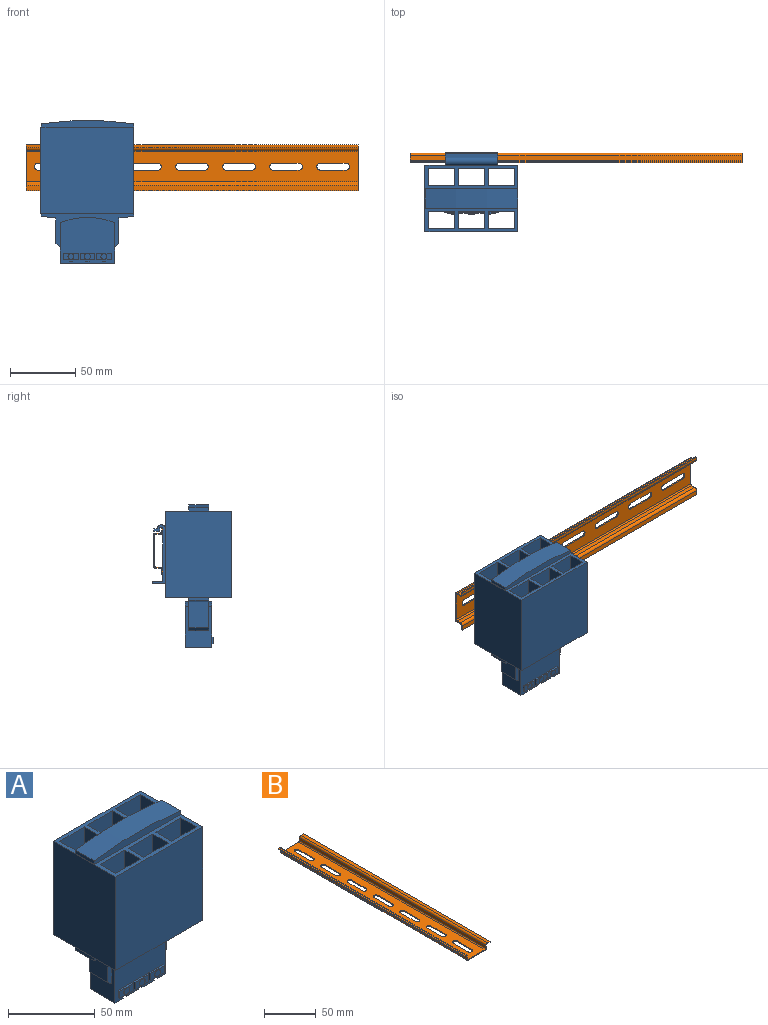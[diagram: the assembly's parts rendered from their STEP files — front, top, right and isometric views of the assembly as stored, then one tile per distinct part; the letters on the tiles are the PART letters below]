
ASSEMBLY  parts=2 mates=1
PART A: 105 faces, bbox 71.1x61x109.2 mm
  f0: cylinder r=246.65mm len=70.61mm, axis (0,-1,0), area 1079.8mm2, adj f9,f10,f11,f12
  f1: plane 40.01x1.91mm, normal (0,1,0), area 76.2mm2, adj f2,f13,f14,f15
  f2: plane 40.01x8.26mm, normal (0,0,1), area 330.2mm2, adj f1,f3,f13,f15
  f3: plane 40.01x40.01mm, normal (0,1,0), area 1600.4mm2, adj f2,f4,f13,f15
  f4: cylinder r=1.27mm len=40.01mm, axis (-1,0,0), area 159.6mm2, adj f3,f5,f13,f15
  f5: plane 40.01x1.91mm, normal (0,-1,0), area 76.2mm2, adj f4,f6,f13,f15
  f6: plane 40.01x4.45mm, normal (0,0,-1), area 177.8mm2, adj f5,f7,f13,f15
  f7: plane 40.01x1.91mm, normal (0,1,0), area 76.2mm2, adj f6,f8,f13,f15
  f8: plane 40.01x2.54mm, normal (0,0,1), area 101.6mm2, adj f7,f13,f15,f16
  f9: plane 70.61x5.08mm, normal (0,1,0), area 299mm2, adj f0,f10,f12,f17
  f10: plane 15.24x2.54mm, normal (-1,0,0), area 38.7mm2, adj f0,f9,f11,f17
  f11: plane 70.61x5.08mm, normal (0,-1,0), area 299mm2, adj f0,f10,f12,f17
  f12: plane 15.24x2.54mm, normal (1,0,0), area 38.7mm2, adj f0,f9,f11,f17
  f13: plane 45.09x10.16mm, normal (1,0,0), area 117.3mm2, adj f1,f2,f3,f4,f5,f6,f7,f8
  f14: plane 40.01x10.16mm, normal (0,0,-1), area 406.5mm2, adj f1,f13,f15,f20
  f15: plane 45.09x10.16mm, normal (-1,0,0), area 117.3mm2, adj f1,f2,f3,f4,f5,f6,f7,f8
  f16: cylinder r=3.17mm len=40.01mm, axis (-1,0,0), area 399mm2, adj f8,f13,f15,f20
  f17: plane 71.12x50.8mm, normal (0,0,1), area 988.4mm2, adj f9,f10,f11,f12,f20,f21,f22,f23
  f18: plane 4.57x4.57mm, normal (0,-1,0), area 16.4mm2, adj f48
  f19: plane 4.57x4.57mm, normal (0,-1,0), area 16.4mm2, adj f49
  f20: plane 71.12x66.04mm, normal (0,1,0), area 3020.2mm2, adj f13,f14,f15,f16,f17,f21,f23,f54
  f21: plane 66.04x50.8mm, normal (-1,0,0), area 3354.8mm2, adj f17,f20,f22,f54
  f22: plane 71.12x66.04mm, normal (0,-1,0), area 4696.8mm2, adj f17,f21,f23,f54
  f23: plane 66.04x50.8mm, normal (1,0,0), area 3354.8mm2, adj f17,f20,f22,f54
  f24: plane 66.04x12.7mm, normal (1,0,0), area 838.7mm2, adj f17,f25,f27,f54
  f25: plane 66.04x20.32mm, normal (0,-1,0), area 1341.9mm2, adj f17,f24,f26,f54
  f26: plane 66.04x12.7mm, normal (-1,0,0), area 838.7mm2, adj f17,f25,f27,f54
  f27: plane 66.04x20.32mm, normal (0,1,0), area 1341.9mm2, adj f17,f24,f26,f54
  f28: plane 66.04x12.7mm, normal (1,0,0), area 838.7mm2, adj f17,f29,f31,f54
  f29: plane 66.04x20.32mm, normal (0,-1,0), area 1341.9mm2, adj f17,f28,f30,f54
  f30: plane 66.04x12.7mm, normal (-1,0,0), area 838.7mm2, adj f17,f29,f31,f54
  f31: plane 66.04x20.32mm, normal (0,1,0), area 1341.9mm2, adj f17,f28,f30,f54
  f32: plane 66.04x12.7mm, normal (1,0,0), area 838.7mm2, adj f17,f33,f35,f54
  f33: plane 66.04x20.32mm, normal (0,-1,0), area 1341.9mm2, adj f17,f32,f34,f54
  f34: plane 66.04x12.7mm, normal (-1,0,0), area 838.7mm2, adj f17,f33,f35,f54
  f35: plane 66.04x20.32mm, normal (0,1,0), area 1341.9mm2, adj f17,f32,f34,f54
  f36: plane 66.04x12.7mm, normal (1,0,0), area 838.7mm2, adj f17,f37,f39,f54
  f37: plane 66.04x20.32mm, normal (0,-1,0), area 1341.9mm2, adj f17,f36,f38,f54
  f38: plane 66.04x12.7mm, normal (-1,0,0), area 838.7mm2, adj f17,f37,f39,f54
  f39: plane 66.04x20.32mm, normal (0,1,0), area 1341.9mm2, adj f17,f36,f38,f54
  f40: plane 66.04x12.7mm, normal (1,0,0), area 838.7mm2, adj f17,f41,f43,f54
  f41: plane 66.04x20.32mm, normal (0,-1,0), area 1341.9mm2, adj f17,f40,f42,f54
  f42: plane 66.04x12.7mm, normal (-1,0,0), area 838.7mm2, adj f17,f41,f43,f54
  f43: plane 66.04x20.32mm, normal (0,1,0), area 1341.9mm2, adj f17,f40,f42,f54
  f44: plane 66.04x12.7mm, normal (1,0,0), area 838.7mm2, adj f17,f45,f47,f54
  f45: plane 66.04x20.32mm, normal (0,-1,0), area 1341.9mm2, adj f17,f44,f46,f54
  f46: plane 66.04x12.7mm, normal (-1,0,0), area 838.7mm2, adj f17,f45,f47,f54
  f47: plane 66.04x20.32mm, normal (0,1,0), area 1341.9mm2, adj f17,f44,f46,f54
  f48: cylinder r=2.29mm len=4.57mm, axis (0,-1,0), area 3.6mm2, adj f18,f59
  f49: cylinder r=2.29mm len=4.57mm, axis (0,-1,0), area 3.6mm2, adj f19,f60
  f50: plane 15.24x2.55mm, normal (0.66,0,-0.75), area 51.8mm2, adj f51,f67,f68,f69
  f51: plane 19.67x15.24mm, normal (1,0,0), area 299.7mm2, adj f50,f52,f67,f69
  f52: plane 15.24x11.18mm, normal (0.11,0,-0.99), area 171.3mm2, adj f51,f53,f67,f69
  f53: plane 15.24x2.29mm, normal (1,0,0), area 35mm2, adj f52,f54,f67,f69
  f54: plane 71.12x50.8mm, normal (0,0,-1), area 988.4mm2, adj f20,f21,f22,f23,f24,f25,f26,f27
  f55: plane 15.24x2.29mm, normal (-1,0,0), area 35mm2, adj f54,f56,f67,f69
  f56: plane 15.24x11.18mm, normal (-0.11,0,-0.99), area 171.3mm2, adj f55,f57,f67,f69
  f57: plane 19.67x15.24mm, normal (-1,0,0), area 299.7mm2, adj f56,f58,f67,f69
  f58: plane 15.24x2.55mm, normal (-0.66,0,-0.75), area 51.8mm2, adj f57,f65,f67,f69
  f59: plane 11.32x5.08mm, normal (0,-1,0), area 41.1mm2, adj f48,f76,f77,f78,f79
  f60: plane 11.32x5.08mm, normal (0,-1,0), area 41.1mm2, adj f49,f80,f81,f82,f83
  f61: plane 2.54x2.54mm, normal (0,1,0), area 6.5mm2, adj f62,f84,f85,f86
  f62: plane 2.54x2.54mm, normal (0,0,-1), area 6.5mm2, adj f61,f72,f84,f86
  f63: plane 2.54x2.54mm, normal (0,1,0), area 6.5mm2, adj f64,f87,f88,f89
  f64: plane 2.54x2.54mm, normal (0,0,-1), area 6.5mm2, adj f63,f71,f87,f89
  f65: plane 15.24x0.8mm, normal (0,0,-1), area 12.1mm2, adj f58,f67,f69,f90
  f66: cylinder r=57.07mm len=41.58mm, axis (0,-1,0), area 108.1mm2, adj f69,f70,f90,f92
  f67: plane 70.61x25.4mm, normal (0,-1,0), area 411.7mm2, adj f50,f51,f52,f53,f54,f55,f56,f57
  f68: plane 15.24x0.8mm, normal (0,0,-1), area 12.1mm2, adj f50,f67,f69,f92
  f69: plane 70.61x25.4mm, normal (0,1,0), area 411.7mm2, adj f50,f51,f52,f53,f54,f55,f56,f57
  f70: plane 41.58x34.98mm, normal (0,1,0), area 1401mm2, adj f66,f90,f92,f93
  f71: plane 3.81x2.54mm, normal (0,-1,0), area 9.7mm2, adj f64,f87,f89,f93
  f72: plane 3.81x2.54mm, normal (0,-1,0), area 9.7mm2, adj f62,f84,f86,f93
  f73: plane 2.54x2.54mm, normal (0,1,0), area 6.5mm2, adj f74,f94,f95,f96
  f74: plane 2.54x2.54mm, normal (0,0,-1), area 6.5mm2, adj f73,f75,f94,f96
  f75: plane 3.81x2.54mm, normal (0,-1,0), area 9.7mm2, adj f74,f93,f94,f96
  f76: plane 5.08x1.27mm, normal (1,0,0), area 6.5mm2, adj f59,f77,f79,f97
  f77: plane 11.32x1.27mm, normal (0,0,1), area 14.4mm2, adj f59,f76,f78,f97
  f78: plane 5.08x1.27mm, normal (-1,0,0), area 6.5mm2, adj f59,f77,f79,f97
  f79: plane 11.32x1.27mm, normal (0,0,-1), area 14.4mm2, adj f59,f76,f78,f97
  f80: plane 5.08x1.27mm, normal (1,0,0), area 6.5mm2, adj f60,f81,f83,f97
  f81: plane 11.32x1.27mm, normal (0,0,1), area 14.4mm2, adj f60,f80,f82,f97
  f82: plane 5.08x1.27mm, normal (-1,0,0), area 6.5mm2, adj f60,f81,f83,f97
  f83: plane 11.32x1.27mm, normal (0,0,-1), area 14.4mm2, adj f60,f80,f82,f97
  f84: plane 15.24x3.81mm, normal (-1,0,0), area 25.8mm2, adj f61,f62,f72,f85,f93,f97
  f85: plane 12.7x2.54mm, normal (0,0,-1), area 32.3mm2, adj f61,f84,f86,f97
  f86: plane 15.24x3.81mm, normal (1,0,0), area 25.8mm2, adj f61,f62,f72,f85,f93,f97
  f87: plane 15.24x3.81mm, normal (-1,0,0), area 25.8mm2, adj f63,f64,f71,f88,f93,f97
  f88: plane 12.7x2.54mm, normal (0,0,-1), area 32.3mm2, adj f63,f87,f89,f97
  f89: plane 15.24x3.81mm, normal (1,0,0), area 25.8mm2, adj f63,f64,f71,f88,f93,f97
  f90: plane 31.06x20.32mm, normal (-1,0,0), area 351.3mm2, adj f65,f66,f67,f69,f70,f91,f93,f97
  f91: cylinder r=57.07mm len=41.58mm, axis (0,-1,0), area 108.1mm2, adj f67,f90,f92,f97
  f92: plane 31.06x20.32mm, normal (1,0,0), area 351.3mm2, adj f66,f67,f68,f69,f70,f91,f93,f97
  f93: plane 41.58x20.32mm, normal (0,0,-1), area 728.7mm2, adj f70,f71,f72,f75,f84,f86,f87,f89
  f94: plane 15.24x3.81mm, normal (-1,0,0), area 25.8mm2, adj f73,f74,f75,f93,f95,f97
  f95: plane 12.7x2.54mm, normal (0,0,-1), area 32.3mm2, adj f73,f94,f96,f97
  f96: plane 15.24x3.81mm, normal (1,0,0), area 25.8mm2, adj f73,f74,f75,f93,f95,f97
  f97: plane 41.58x34.98mm, normal (0,-1,0), area 1218.8mm2, adj f76,f77,f78,f79,f80,f81,f82,f83
  f98: plane 11.32x1.27mm, normal (0,0,1), area 14.4mm2, adj f97,f99,f101,f103
  f99: plane 5.08x1.27mm, normal (1,0,0), area 6.5mm2, adj f97,f98,f100,f103
  f100: plane 11.32x1.27mm, normal (0,0,-1), area 14.4mm2, adj f97,f99,f101,f103
  f101: plane 5.08x1.27mm, normal (-1,0,0), area 6.5mm2, adj f97,f98,f100,f103
  f102: plane 4.57x4.57mm, normal (0,-1,0), area 16.4mm2, adj f104
  f103: plane 11.32x5.08mm, normal (0,-1,0), area 41.1mm2, adj f98,f99,f100,f101,f104
  f104: cylinder r=2.29mm len=4.57mm, axis (0,-1,0), area 3.6mm2, adj f102,f103
PART B: 50 faces, bbox 35x254x7.5 mm
  f0: cylinder r=1mm len=254mm, axis (0,1,0), area 399.3mm2, adj f1,f19,f20,f21
  f1: plane 254x3.5mm, normal (1,0,0), area 889mm2, adj f0,f2,f20,f21
  f2: cylinder r=2mm len=254mm, axis (0,1,0), area 797.6mm2, adj f1,f3,f20,f21
  f3: plane 254x2.19mm, normal (0,0,1), area 556.3mm2, adj f2,f4,f20,f21
  f4: plane 254x1mm, normal (-1,0,0), area 254.2mm2, adj f3,f5,f20,f21
  f5: plane 254x2.17mm, normal (0,0,-1), area 551.7mm2, adj f4,f6,f20,f21
  f6: cylinder r=1mm len=254mm, axis (0,1,0), area 399.3mm2, adj f5,f7,f20,f21
  f7: plane 254x3.5mm, normal (-1,0,0), area 889mm2, adj f6,f8,f20,f21
  f8: cylinder r=2mm len=254mm, axis (0,1,0), area 797.6mm2, adj f7,f9,f20,f21
  f9: plane 254x23mm, normal (0,0,-1), area 4973.3mm2, adj f8,f10,f20,f21,f22,f23,f24,f25
  f10: cylinder r=2mm len=254mm, axis (0,1,0), area 797.6mm2, adj f9,f11,f20,f21
  f11: plane 254x3.5mm, normal (1,0,0), area 889mm2, adj f10,f12,f20,f21
  f12: cylinder r=1mm len=254mm, axis (0,1,0), area 399.3mm2, adj f11,f13,f20,f21
  f13: plane 254x3.83mm, normal (0,0,-1), area 972.1mm2, adj f12,f14,f20,f21
  f14: plane 254x1mm, normal (1,0,0), area 254.2mm2, adj f13,f15,f20,f21
  f15: plane 254x3.81mm, normal (0,0,1), area 968.3mm2, adj f14,f16,f20,f21
  f16: cylinder r=2mm len=254mm, axis (0,1,0), area 797.6mm2, adj f15,f17,f20,f21
  f17: plane 254x3.5mm, normal (-1,0,0), area 889mm2, adj f16,f18,f20,f21
  f18: cylinder r=1mm len=254mm, axis (0,1,0), area 399.3mm2, adj f17,f19,f20,f21
  f19: plane 254x23mm, normal (0,0,1), area 4972.7mm2, adj f0,f18,f20,f21,f22,f23,f24,f25
  f20: plane 35x7.5mm, normal (0,-1,0), area 45.5mm2, adj f0,f1,f2,f3,f4,f5,f6,f7
  f21: plane 35x7.5mm, normal (0,1,0), area 45.5mm2, adj f0,f1,f2,f3,f4,f5,f6,f7
  f22: cylinder r=2.6mm len=5.2mm, axis (0,0,1), area 8.2mm2, adj f9,f19,f23,f25
  f23: plane 19.8x1mm, normal (1,0,0), area 19.8mm2, adj f9,f19,f22,f24
  f24: cylinder r=2.6mm len=5.2mm, axis (0,0,1), area 8.2mm2, adj f9,f19,f23,f25
  f25: plane 19.8x1mm, normal (-1,0,0), area 19.8mm2, adj f9,f19,f22,f24
  f26: plane 19.8x1mm, normal (-1,0,0), area 19.8mm2, adj f9,f19,f27,f29
  f27: cylinder r=2.6mm len=5.2mm, axis (0,0,1), area 8.2mm2, adj f9,f19,f26,f28
  f28: plane 19.8x1mm, normal (1,0,0), area 19.8mm2, adj f9,f19,f27,f29
  f29: cylinder r=2.6mm len=5.2mm, axis (0,0,1), area 8.2mm2, adj f9,f19,f26,f28
  f30: cylinder r=2.6mm len=5.2mm, axis (0,0,1), area 8.2mm2, adj f9,f19,f31,f33
  f31: plane 19.8x1mm, normal (1,0,0), area 19.8mm2, adj f9,f19,f30,f32
  f32: cylinder r=2.6mm len=5.2mm, axis (0,0,1), area 8.2mm2, adj f9,f19,f31,f33
  f33: plane 19.8x1mm, normal (-1,0,0), area 19.8mm2, adj f9,f19,f30,f32
  f34: cylinder r=2.6mm len=5.2mm, axis (0,0,1), area 8.2mm2, adj f9,f19,f35,f37
  f35: plane 19.8x1mm, normal (1,0,0), area 19.8mm2, adj f9,f19,f34,f36
  f36: cylinder r=2.6mm len=5.2mm, axis (0,0,1), area 8.2mm2, adj f9,f19,f35,f37
  f37: plane 19.8x1mm, normal (-1,0,0), area 19.8mm2, adj f9,f19,f34,f36
  f38: cylinder r=2.6mm len=5.2mm, axis (0,0,1), area 8.2mm2, adj f9,f19,f39,f41
  f39: plane 19.8x1mm, normal (1,0,0), area 19.8mm2, adj f9,f19,f38,f40
  f40: cylinder r=2.6mm len=5.2mm, axis (0,0,1), area 8.2mm2, adj f9,f19,f39,f41
  f41: plane 19.8x1mm, normal (-1,0,0), area 19.8mm2, adj f9,f19,f38,f40
  f42: cylinder r=2.6mm len=5.2mm, axis (0,0,1), area 8.2mm2, adj f9,f19,f43,f45
  f43: plane 19.8x1mm, normal (1,0,0), area 19.8mm2, adj f9,f19,f42,f44
  f44: cylinder r=2.6mm len=5.2mm, axis (0,0,1), area 8.2mm2, adj f9,f19,f43,f45
  f45: plane 19.8x1mm, normal (-1,0,0), area 19.8mm2, adj f9,f19,f42,f44
  f46: cylinder r=2.6mm len=5.2mm, axis (0,0,1), area 8.2mm2, adj f9,f19,f47,f49
  f47: plane 19.8x1mm, normal (1,0,0), area 19.8mm2, adj f9,f19,f46,f48
  f48: cylinder r=2.6mm len=5.2mm, axis (0,0,1), area 8.2mm2, adj f9,f19,f47,f49
  f49: plane 19.8x1mm, normal (-1,0,0), area 19.8mm2, adj f9,f19,f46,f48
PLACE A t=(-80,-34.81,-35.71)mm
PLACE B rot(axis=(0.58,0.58,-0.58),120deg) t=(0,0,0)mm
MATE fastened A.f3 <-> B.f3  axis (0,1,0) through (-80,-7.5,16.67)mm
